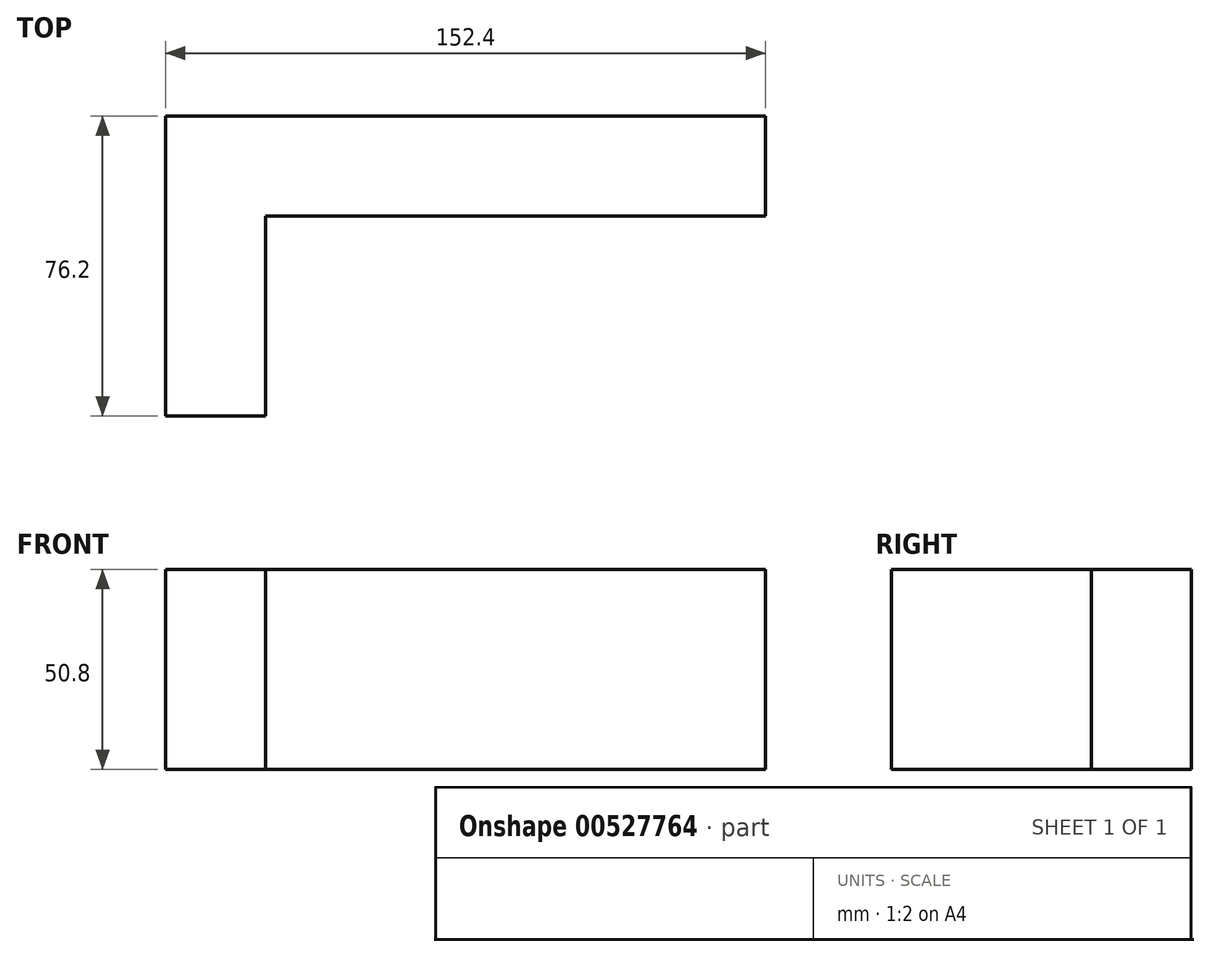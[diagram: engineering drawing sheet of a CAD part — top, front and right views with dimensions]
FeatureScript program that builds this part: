
annotation { "Feature Type Name" : "Feature", "Feature Type Description" : "" }
export const myFeature = defineFeature(function(context is Context, id is Id, definition is map)
    precondition{}
    {
        {
            var Q0;
            Q0=qCreatedBy(makeId("Top.planeOp"),FACE);
            var sketch = newSketch(context, id + "F0", { "sketchPlane" : qUnion([Q0])});
            skLineSegment(sketch, "E0", {"start": v(-53.51, -50.8) * mm, "end": v(-53.51, 25.4) * mm});
            skLineSegment(sketch, "E1", {"start": v(-53.51, 25.4) * mm, "end": v(98.89, 25.4) * mm});
            skLineSegment(sketch, "E2", {"start": v(98.89, 25.4) * mm, "end": v(98.89, 0) * mm});
            skLineSegment(sketch, "E3", {"start": v(98.89, 0) * mm, "end": v(-28.11, 0) * mm});
            skLineSegment(sketch, "E4", {"start": v(-28.11, 0) * mm, "end": v(-28.11, -50.8) * mm});
            skLineSegment(sketch, "E5", {"start": v(-28.11, -50.8) * mm, "end": v(-53.51, -50.8) * mm});
            skSolve(sketch);
        }
        {
            var Q0;
            Q0=makeQuery(id+"F0.imprint","IMPRINT",FACE,{"disambiguationData":[TD([[makeQuery(id+"F0.imprint","IMPRINT",EDGE,{"derivedFrom":sQuery(id+"F0.wireOp",EDGE,"E0")}),-1.0]])]});
            var sketch = newSketch(context, id + "F1", { "sketchPlane" : qUnion([Q0])});
            skLineSegment(sketch, "E6.bottom", {"start": v(48.09, 25.4) * mm, "end": v(98.89, 25.4) * mm});
            skLineSegment(sketch, "E6.top", {"start": v(48.09, 0) * mm, "end": v(98.89, 0) * mm});
            skLineSegment(sketch, "E6.left", {"start": v(48.09, 25.4) * mm, "end": v(48.09, 0) * mm});
            skLineSegment(sketch, "E6.right", {"start": v(98.89, 25.4) * mm, "end": v(98.89, 0) * mm});
            skSolve(sketch);
        }
        {
            var Q0;
            Q0 = qSketchRegion(id + "F1", true);
            extrude(context, id + "F2", {"entities" : qUnion([Q0]), "depth" : 25.4 * mm, "offsetDistance" : 25.4 * mm});
        }
        {
            var Q0;
            Q0=makeQuery(id+"F0.imprint","IMPRINT",FACE,{"disambiguationData":[TD([[makeQuery(id+"F0.imprint","IMPRINT",EDGE,{"derivedFrom":sQuery(id+"F0.wireOp",EDGE,"E0")}),-1.0]])]});
            extrude(context, id + "F3", {"entities" : qUnion([Q0]), "operationType" : NewBodyOperationType.ADD, "depth" : 50.8 * mm, "offsetDistance" : 25.4 * mm});
        }
    });
